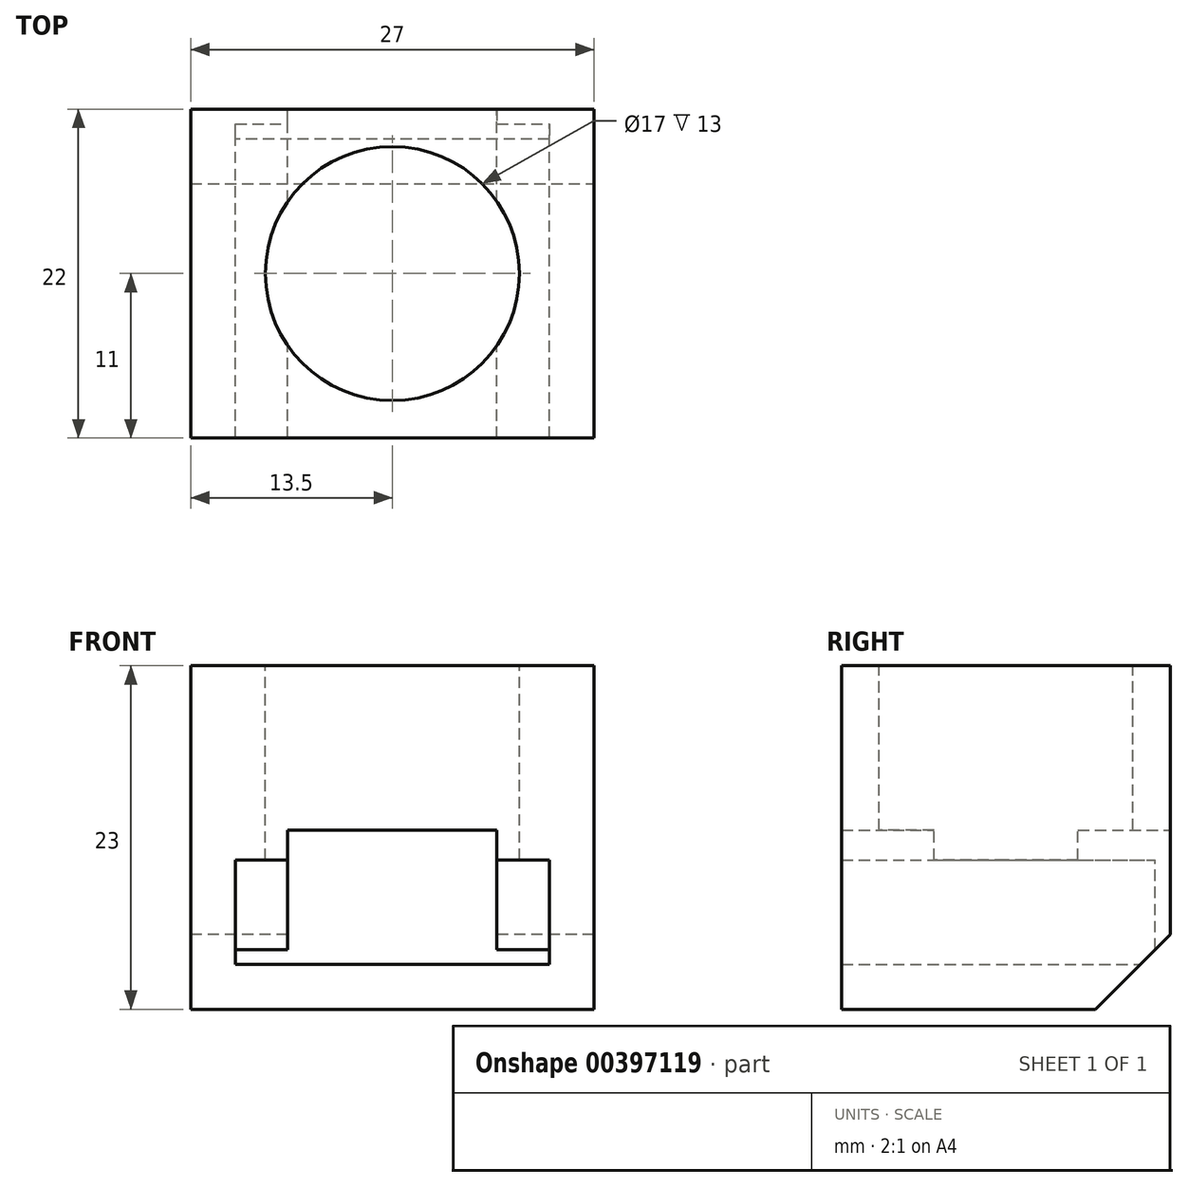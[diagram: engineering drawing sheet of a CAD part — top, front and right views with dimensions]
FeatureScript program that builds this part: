
annotation { "Feature Type Name" : "Feature", "Feature Type Description" : "" }
export const myFeature = defineFeature(function(context is Context, id is Id, definition is map)
    precondition{}
    {
        {
            var Q0;
            Q0=qCreatedBy(makeId("Top.planeOp"),FACE);
            var sketch = newSketch(context, id + "F0", { "sketchPlane" : qUnion([Q0])});
            skLineSegment(sketch, "E0.bottom", {"start": v(13.5, -11) * mm, "end": v(-13.5, -11) * mm});
            skLineSegment(sketch, "E0.top", {"start": v(13.5, 11) * mm, "end": v(-13.5, 11) * mm});
            skLineSegment(sketch, "E0.left", {"start": v(13.5, -11) * mm, "end": v(13.5, 11) * mm});
            skLineSegment(sketch, "E0.right", {"start": v(-13.5, -11) * mm, "end": v(-13.5, 11) * mm});
            skPoint(sketch, "E0.middle", {"position": v(0, 0) * mm});
            skSolve(sketch);
        }
        {
            var Q0;
            Q0=qSketchRegion(id+"F0",true);
            extrude(context, id + "F1", {"entities" : qUnion([Q0]), "depth" : 20 * mm});
        }
        {
            var Q0;
            Q0=makeQuery(id+"F1.opExtrude","CAP_FACE",FACE,{"disambiguationData":[OSD([sQuery(id+"F0.wireOp",EDGE,"E0.bottom"),sQuery(id+"F0.wireOp",EDGE,"E0.top"),sQuery(id+"F0.wireOp",EDGE,"E0.left"),sQuery(id+"F0.wireOp",EDGE,"E0.right")])],"isStart":true});
            var sketch = newSketch(context, id + "F2", { "sketchPlane" : qUnion([Q0])});
            skLineSegment(sketch, "E1", {"start": v(-13.5, 11) * mm, "end": v(-10.5, 11) * mm});
            skLineSegment(sketch, "E2.bottom", {"start": v(-10.5, 11) * mm, "end": v(10.5, 11) * mm});
            skLineSegment(sketch, "E2.top", {"start": v(-10.5, -10) * mm, "end": v(10.5, -10) * mm});
            skLineSegment(sketch, "E2.left", {"start": v(-10.5, 11) * mm, "end": v(-10.5, -10) * mm});
            skLineSegment(sketch, "E2.right", {"start": v(10.5, 11) * mm, "end": v(10.5, -10) * mm});
            skSolve(sketch);
        }
        {
            var Q0;
            Q0=qSketchRegion(id+"F2",true);
            extrude(context, id + "F3", {"entities" : qUnion([Q0]), "operationType" : NewBodyOperationType.REMOVE, "oppositeDirection" : true, "depth" : 6 * mm});
        }
        {
            var Q0;
            Q0=makeQuery(id+"F3.boolean.opBoolean","COPY",FACE,{"derivedFrom":makeQuery(id+"F3.opExtrude","CAP_FACE",FACE,{"disambiguationData":[OSD([sQuery(id+"F2.wireOp",EDGE,"E2.bottom"),sQuery(id+"F2.wireOp",EDGE,"E2.top"),sQuery(id+"F2.wireOp",EDGE,"E2.left"),sQuery(id+"F2.wireOp",EDGE,"E2.right")])],"isStart":false})});
            var sketch = newSketch(context, id + "F4", { "sketchPlane" : qUnion([Q0])});
            skLineSegment(sketch, "E3", {"start": v(-10.5, 11) * mm, "end": v(0, 11) * mm});
            skLineSegment(sketch, "E4", {"start": v(0, 11) * mm, "end": v(0, 0) * mm});
            skLineSegment(sketch, "E5.bottom", {"start": v(7, 11) * mm, "end": v(-7, 11) * mm});
            skLineSegment(sketch, "E5.top", {"start": v(7, -11) * mm, "end": v(-7, -11) * mm});
            skLineSegment(sketch, "E5.left", {"start": v(7, 11) * mm, "end": v(7, -11) * mm});
            skLineSegment(sketch, "E5.right", {"start": v(-7, 11) * mm, "end": v(-7, -11) * mm});
            skPoint(sketch, "E5.middle", {"position": v(0, 0) * mm});
            skSolve(sketch);
        }
        {
            var Q0;
            Q0=qSketchRegion(id+"F4",true);
            extrude(context, id + "F5", {"entities" : qUnion([Q0]), "operationType" : NewBodyOperationType.REMOVE, "oppositeDirection" : true, "depth" : 2 * mm});
        }
        {
            var Q0;
            Q0=makeQuery(id+"F1.opExtrude","CAP_FACE",FACE,{"disambiguationData":[OSD([sQuery(id+"F0.wireOp",EDGE,"E0.bottom"),sQuery(id+"F0.wireOp",EDGE,"E0.top"),sQuery(id+"F0.wireOp",EDGE,"E0.left"),sQuery(id+"F0.wireOp",EDGE,"E0.right")])],"isStart":false});
            var sketch = newSketch(context, id + "F6", { "sketchPlane" : qUnion([Q0])});
            skLineSegment(sketch, "E6", {"start": v(0, -11) * mm, "end": v(0, -0.5) * mm});
            skPoint(sketch, "E6.endSnap0", {"position": v(0, -11) * mm});
            skLineSegment(sketch, "E7.bottom", {"start": v(3, -3) * mm, "end": v(-3, -3) * mm});
            skLineSegment(sketch, "E7.top", {"start": v(3, 3) * mm, "end": v(-3, 3) * mm});
            skLineSegment(sketch, "E7.left", {"start": v(3, -3) * mm, "end": v(3, 3) * mm});
            skLineSegment(sketch, "E7.right", {"start": v(-3, -3) * mm, "end": v(-3, 3) * mm});
            skPoint(sketch, "E7.middle", {"position": v(0, 0) * mm});
            skSolve(sketch);
        }
        {
            var Q0;
            Q0=qSketchRegion(id+"F6",true);
            extrude(context, id + "F7", {"entities" : qUnion([Q0]), "operationType" : NewBodyOperationType.REMOVE, "oppositeDirection" : true, "depth" : 20 * mm});
        }
        {
            var Q0;
            Q0=makeQuery(id+"F5.boolean.opBoolean","COPY",FACE,{"derivedFrom":makeQuery(id+"F5.opExtrude","CAP_FACE",FACE,{"disambiguationData":[OSD([sQuery(id+"F4.wireOp",EDGE,"E5.bottom"),sQuery(id+"F4.wireOp",EDGE,"E5.top"),sQuery(id+"F4.wireOp",EDGE,"E5.left"),sQuery(id+"F4.wireOp",EDGE,"E5.right")])],"isStart":true})});
            extrude(context, id + "F8", {"entities" : qUnion([Q0]), "operationType" : NewBodyOperationType.REMOVE, "oppositeDirection" : true, "depth" : 6 * mm});
        }
        {
            var Q0;
            {var subQ0=sQuery(id+"F0.wireOp",EDGE,"E0.top");var subQ1=sQuery(id+"F0.wireOp",EDGE,"E0.right");var subQ2=sQuery(id+"F0.wireOp",EDGE,"E0.bottom");Q0=makeQuery(id+"F8.boolean.opBoolean","SPLIT",FACE,{"disambiguationData":[TD([makeQuery(id+"F1.opExtrude","SWEPT_FACE",FACE,{"disambiguationData":[OSD([subQ1])]})])],"derivedFrom":makeQuery(id+"F1.opExtrude","CAP_FACE",FACE,{"disambiguationData":[OSD([subQ2,subQ0,sQuery(id+"F0.wireOp",EDGE,"E0.left"),subQ1])],"isStart":true})});}
            var sketch = newSketch(context, id + "F9", { "sketchPlane" : qUnion([Q0])});
            skLineSegment(sketch, "E8.bottom", {"start": v(-13.5, -11) * mm, "end": v(13.5, -11) * mm});
            skLineSegment(sketch, "E8.top", {"start": v(-13.5, 11) * mm, "end": v(13.5, 11) * mm});
            skLineSegment(sketch, "E8.left", {"start": v(-13.5, -11) * mm, "end": v(-13.5, 11) * mm});
            skLineSegment(sketch, "E8.right", {"start": v(13.5, -11) * mm, "end": v(13.5, 11) * mm});
            skSolve(sketch);
        }
        {
            var Q0;
            Q0=qSketchRegion(id+"F9",true);
            extrude(context, id + "F10", {"entities" : qUnion([Q0]), "operationType" : NewBodyOperationType.ADD, "depth" : 3 * mm});
        }
        {
            var Q0;
            Q0=makeQuery(id+"F10.opExtrude","CAP_EDGE",EDGE,{"disambiguationData":[OSD([sQuery(id+"F9.wireOp",EDGE,"E8.bottom")])],"isStart":false});
            chamfer(context, id + "F11", {"entities" : qUnion([Q0]), "width" : 5 * mm, "tangentPropagation" : true});
        }
        {
            var Q0;
            Q0=makeQuery(id+"F1.opExtrude","CAP_FACE",FACE,{"disambiguationData":[OSD([sQuery(id+"F0.wireOp",EDGE,"E0.bottom"),sQuery(id+"F0.wireOp",EDGE,"E0.top"),sQuery(id+"F0.wireOp",EDGE,"E0.left"),sQuery(id+"F0.wireOp",EDGE,"E0.right")])],"isStart":false});
            var sketch = newSketch(context, id + "F12", { "sketchPlane" : qUnion([Q0])});
            skCircle(sketch, "E9", {"center": v(0, 0) * mm, "radius": 8.5 * mm});
            skSolve(sketch);
        }
        {
            var Q0;
            Q0 = qSketchRegion(id + "F12", true);
            extrude(context, id + "F13", {"entities" : qUnion([Q0]), "operationType" : NewBodyOperationType.REMOVE, "oppositeDirection" : true, "depth" : 20 * mm});
        }
        {
            var Q0;
            {var subQ1=sQuery(id+"F2.wireOp",EDGE,"E2.left");var subQ2=sQuery(id+"F2.wireOp",EDGE,"E2.top");Q0=makeQuery(id+"F5.boolean.opBoolean","SPLIT",FACE,{"disambiguationData":[TD([makeQuery(id+"F3.boolean.opBoolean","COPY",FACE,{"derivedFrom":makeQuery(id+"F3.opExtrude","SWEPT_FACE",FACE,{"disambiguationData":[OSD([subQ1])]})})])],"derivedFrom":makeQuery(id+"F3.boolean.opBoolean","COPY",FACE,{"derivedFrom":makeQuery(id+"F3.opExtrude","CAP_FACE",FACE,{"disambiguationData":[OSD([sQuery(id+"F2.wireOp",EDGE,"E2.bottom"),subQ2,subQ1,sQuery(id+"F2.wireOp",EDGE,"E2.right")])],"isStart":false})})});}
            var Q1;
            {var subQ1=sQuery(id+"F2.wireOp",EDGE,"E2.right");var subQ2=sQuery(id+"F2.wireOp",EDGE,"E2.top");Q1=makeQuery(id+"F5.boolean.opBoolean","SPLIT",FACE,{"disambiguationData":[TD([makeQuery(id+"F3.boolean.opBoolean","COPY",FACE,{"derivedFrom":makeQuery(id+"F3.opExtrude","SWEPT_FACE",FACE,{"disambiguationData":[OSD([subQ1])]})})])],"derivedFrom":makeQuery(id+"F3.boolean.opBoolean","COPY",FACE,{"derivedFrom":makeQuery(id+"F3.opExtrude","CAP_FACE",FACE,{"disambiguationData":[OSD([sQuery(id+"F2.wireOp",EDGE,"E2.bottom"),subQ2,sQuery(id+"F2.wireOp",EDGE,"E2.left"),subQ1])],"isStart":false})})});}
            var Q2;
            {var subQ0=sQuery(id+"F4.wireOp",EDGE,"E5.right");var subQ1=sQuery(id+"F4.wireOp",EDGE,"E5.left");Q2=makeQuery(id+"F13.boolean.opBoolean","SPLIT",FACE,{"disambiguationData":[TD([makeQuery(id+"F1.opExtrude","SWEPT_FACE",FACE,{"disambiguationData":[OSD([sQuery(id+"F0.wireOp",EDGE,"E0.bottom")])]})])],"derivedFrom":makeQuery(id+"F5.boolean.opBoolean","COPY",FACE,{"derivedFrom":makeQuery(id+"F5.opExtrude","CAP_FACE",FACE,{"disambiguationData":[OSD([sQuery(id+"F4.wireOp",EDGE,"E5.bottom"),sQuery(id+"F4.wireOp",EDGE,"E5.top"),subQ1,subQ0])],"isStart":false})})});}
            var Q3;
            {var subQ0=sQuery(id+"F4.wireOp",EDGE,"E5.right");var subQ1=sQuery(id+"F4.wireOp",EDGE,"E5.left");Q3=makeQuery(id+"F13.boolean.opBoolean","SPLIT",FACE,{"disambiguationData":[TD([makeQuery(id+"F1.opExtrude","SWEPT_FACE",FACE,{"disambiguationData":[OSD([sQuery(id+"F0.wireOp",EDGE,"E0.top")])]})])],"derivedFrom":makeQuery(id+"F5.boolean.opBoolean","COPY",FACE,{"derivedFrom":makeQuery(id+"F5.opExtrude","CAP_FACE",FACE,{"disambiguationData":[OSD([sQuery(id+"F4.wireOp",EDGE,"E5.bottom"),sQuery(id+"F4.wireOp",EDGE,"E5.top"),subQ1,subQ0])],"isStart":false})})});}
            extrude(context, id + "F14", {"entities" : qUnion([Q0, Q1, Q2, Q3]), "operationType" : NewBodyOperationType.REMOVE, "oppositeDirection" : true, "depth" : 1 * mm});
        }
    });
